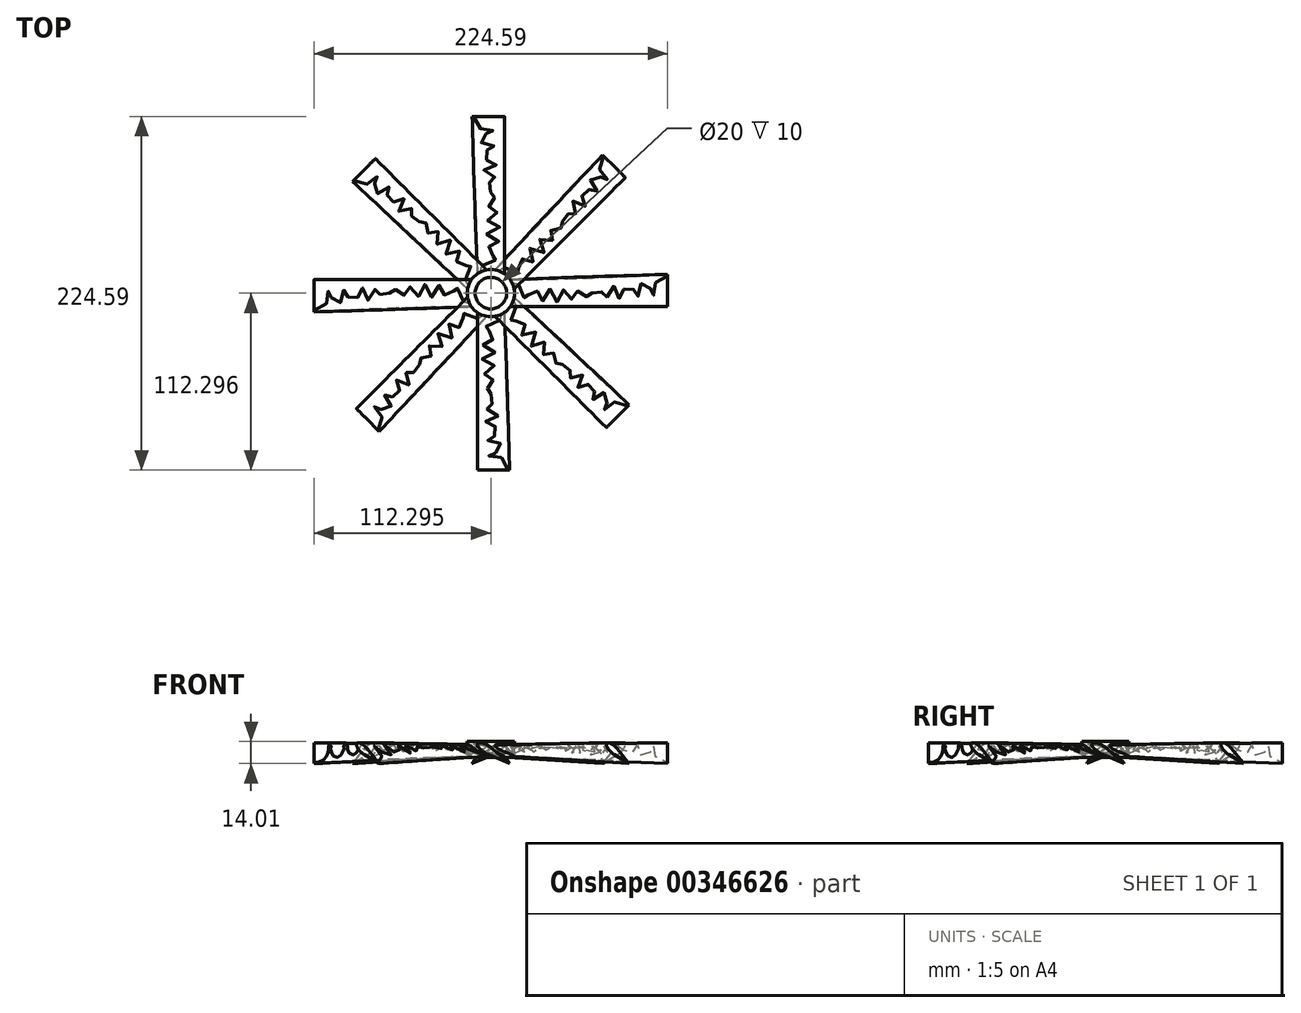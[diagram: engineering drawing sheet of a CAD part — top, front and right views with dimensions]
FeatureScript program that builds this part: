
annotation { "Feature Type Name" : "Feature", "Feature Type Description" : "" }
export const myFeature = defineFeature(function(context is Context, id is Id, definition is map)
    precondition{}
    {
        {
            var Q0;
            Q0=qCreatedBy(makeId("Right.planeOp"),FACE);
            var sketch = newSketch(context, id + "F0", { "sketchPlane" : qUnion([Q0])});
            skCircle(sketch, "E0", {"center": v(0, 0) * mm, "radius": 5 * mm});
            skPoint(sketch, "E1", {"position": v(3.38, 3.68) * mm});
            skPoint(sketch, "E2", {"position": v(-2.55, 4.3) * mm});
            skPoint(sketch, "E3", {"position": v(-4.58, 2) * mm});
            skPoint(sketch, "E4", {"position": v(-3.59, -3.48) * mm});
            skPoint(sketch, "E5", {"position": v(1.45, -4.79) * mm});
            skLineSegment(sketch, "E6", {"start": v(0, 11.08) * mm, "end": v(0, 16.41) * mm, "construction": true});
            skSolve(sketch);
        }
        {
            var Q0;
            Q0=qCreatedBy(makeId("Right.planeOp"),FACE);
            cPlane(context, id + "F1", {"entities" : qUnion([Q0]), "cplaneType" : CPlaneType.OFFSET, "offset" : 10 * mm, "width" : 150 * mm, "height" : 150 * mm});
        }
        {
            var Q0;
            Q0=qCreatedBy(id+"F1.planeOp",FACE);
            var sketch = newSketch(context, id + "F2", { "sketchPlane" : qUnion([Q0])});
            skCircle(sketch, "E7", {"center": v(0, 0) * mm, "radius": 5 * mm});
            skPoint(sketch, "E8", {"position": v(3.38, 3.68) * mm});
            skPoint(sketch, "E9", {"position": v(-2.55, 4.3) * mm});
            skPoint(sketch, "E10", {"position": v(-4.58, 2) * mm});
            skPoint(sketch, "E11", {"position": v(-3.59, -3.48) * mm});
            skPoint(sketch, "E12", {"position": v(1.45, -4.79) * mm});
            skSolve(sketch);
        }
        {
            var Q0;
            Q0=qCreatedBy(makeId("Right.planeOp"),FACE);
            cPlane(context, id + "F3", {"entities" : qUnion([Q0]), "cplaneType" : CPlaneType.OFFSET, "offset" : 20 * mm, "width" : 150 * mm, "height" : 150 * mm});
        }
        {
            var Q0;
            Q0=qCreatedBy(id+"F3.planeOp",FACE);
            var sketch = newSketch(context, id + "F4", { "sketchPlane" : qUnion([Q0])});
            skLineSegment(sketch, "E13", {"start": v(11.65, 0) * mm, "end": v(19.56, 0) * mm, "construction": true});
            skLineSegment(sketch, "E14", {"start": v(-14.42, -9) * mm, "end": v(5.84, 3.65) * mm, "construction": true});
            skPoint(sketch, "E15", {"position": v(0.08, 0.05) * mm});
            skEllipse(sketch, "E16", {"center": v(0.08, 0.05) * mm, "majorRadius": 6.78 * mm, "minorRadius": 2.5 * mm, "majorAxis": v(0.85, 0.53)});
            skLineSegment(sketch, "E17", {"start": v(0.08, 0.05) * mm, "end": v(-1.24, 2.17) * mm, "construction": true});
            skLineSegment(sketch, "E18", {"start": v(-14.42, -9) * mm, "end": v(-3.41, 0.57) * mm});
            skLineSegment(sketch, "E19", {"start": v(-14.42, -9) * mm, "end": v(-0.98, -3.32) * mm});
            skPoint(sketch, "E20", {"position": v(0, 0) * mm});
            skSolve(sketch);
        }
        {
            var Q0;
            Q0=qCreatedBy(makeId("Right.planeOp"),FACE);
            cPlane(context, id + "F5", {"entities" : qUnion([Q0]), "cplaneType" : CPlaneType.OFFSET, "offset" : 25 * mm, "width" : 150 * mm, "height" : 150 * mm});
        }
        {
            var Q0;
            Q0=qCreatedBy(id+"F5.planeOp",FACE);
            var sketch = newSketch(context, id + "F6", { "sketchPlane" : qUnion([Q0])});
            skLineSegment(sketch, "E21", {"start": v(11.65, 0) * mm, "end": v(19.56, 0) * mm, "construction": true});
            skLineSegment(sketch, "E22", {"start": v(-14.28, -8.75) * mm, "end": v(3.41, 2.09) * mm, "construction": true});
            skPoint(sketch, "E23", {"position": v(0.09, 0.05) * mm});
            skEllipse(sketch, "E24", {"center": v(0.09, 0.05) * mm, "majorRadius": 3.9 * mm, "minorRadius": 2.3 * mm, "majorAxis": v(0.85, 0.52)});
            skLineSegment(sketch, "E25", {"start": v(0.09, 0.05) * mm, "end": v(-1.12, 2.01) * mm, "construction": true});
            skLineSegment(sketch, "E26", {"start": v(-14.28, -8.75) * mm, "end": v(-1.85, 1.49) * mm});
            skLineSegment(sketch, "E27", {"start": v(-14.28, -8.75) * mm, "end": v(0.48, -2.33) * mm});
            skPoint(sketch, "E28", {"position": v(0, 0) * mm});
            skSolve(sketch);
        }
        {
            var Q0;
            Q0=qCreatedBy(makeId("Right.planeOp"),FACE);
            cPlane(context, id + "F7", {"entities" : qUnion([Q0]), "cplaneType" : CPlaneType.OFFSET, "offset" : 30 * mm, "width" : 150 * mm, "height" : 150 * mm});
        }
        {
            var Q0;
            Q0=qCreatedBy(id+"F7.planeOp",FACE);
            var sketch = newSketch(context, id + "F8", { "sketchPlane" : qUnion([Q0])});
            skLineSegment(sketch, "E29", {"start": v(11.65, 0) * mm, "end": v(19.56, 0) * mm, "construction": true});
            skLineSegment(sketch, "E30", {"start": v(-14.14, -8.5) * mm, "end": v(5.57, 3.35) * mm, "construction": true});
            skPoint(sketch, "E31", {"position": v(0.17, 0.1) * mm});
            skEllipse(sketch, "E32", {"center": v(0.17, 0.1) * mm, "majorRadius": 6.3 * mm, "minorRadius": 2.4 * mm, "majorAxis": v(0.86, 0.52)});
            skLineSegment(sketch, "E33", {"start": v(0.17, 0.1) * mm, "end": v(-1.06, 2.16) * mm, "construction": true});
            skLineSegment(sketch, "E34", {"start": v(-14.14, -8.5) * mm, "end": v(-3.01, 0.78) * mm});
            skLineSegment(sketch, "E35", {"start": v(-14.14, -8.5) * mm, "end": v(-0.72, -3.03) * mm});
            skPoint(sketch, "E36", {"position": v(0, 0) * mm});
            skSolve(sketch);
        }
        {
            var Q0;
            Q0=qCreatedBy(makeId("Right.planeOp"),FACE);
            cPlane(context, id + "F9", {"entities" : qUnion([Q0]), "cplaneType" : CPlaneType.OFFSET, "offset" : 35 * mm, "width" : 150 * mm, "height" : 150 * mm});
        }
        {
            var Q0;
            Q0=qCreatedBy(id+"F9.planeOp",FACE);
            var sketch = newSketch(context, id + "F10", { "sketchPlane" : qUnion([Q0])});
            skLineSegment(sketch, "E37", {"start": v(11.65, 0) * mm, "end": v(19.56, 0) * mm, "construction": true});
            skLineSegment(sketch, "E38", {"start": v(-14, -8.25) * mm, "end": v(3.45, 2.03) * mm, "construction": true});
            skPoint(sketch, "E39", {"position": v(0.09, 0.05) * mm});
            skEllipse(sketch, "E40", {"center": v(0.09, 0.05) * mm, "majorRadius": 3.9 * mm, "minorRadius": 2.2 * mm, "majorAxis": v(0.86, 0.5)});
            skLineSegment(sketch, "E41", {"start": v(0.09, 0.05) * mm, "end": v(-1.03, 1.95) * mm, "construction": true});
            skLineSegment(sketch, "E42", {"start": v(-14, -8.25) * mm, "end": v(-1.8, 1.42) * mm});
            skLineSegment(sketch, "E43", {"start": v(-14, -8.25) * mm, "end": v(0.37, -2.26) * mm});
            skPoint(sketch, "E44", {"position": v(0, 0) * mm});
            skSolve(sketch);
        }
        {
            var Q0;
            Q0=qCreatedBy(makeId("Right.planeOp"),FACE);
            cPlane(context, id + "F11", {"entities" : qUnion([Q0]), "cplaneType" : CPlaneType.OFFSET, "offset" : 40 * mm, "width" : 150 * mm, "height" : 150 * mm});
        }
        {
            var Q0;
            Q0=qCreatedBy(id+"F11.planeOp",FACE);
            var sketch = newSketch(context, id + "F12", { "sketchPlane" : qUnion([Q0])});
            skLineSegment(sketch, "E45", {"start": v(11.65, 0) * mm, "end": v(19.56, 0) * mm, "construction": true});
            skLineSegment(sketch, "E46", {"start": v(-13.86, -8) * mm, "end": v(5.63, 3.25) * mm, "construction": true});
            skPoint(sketch, "E47", {"position": v(0.26, 0.15) * mm});
            skEllipse(sketch, "E48", {"center": v(0.26, 0.15) * mm, "majorRadius": 6.2 * mm, "minorRadius": 2.3 * mm, "majorAxis": v(0.87, 0.5)});
            skLineSegment(sketch, "E49", {"start": v(0.26, 0.15) * mm, "end": v(-0.9, 2.14) * mm, "construction": true});
            skLineSegment(sketch, "E50", {"start": v(-13.86, -8) * mm, "end": v(-2.85, 0.81) * mm});
            skLineSegment(sketch, "E51", {"start": v(-13.86, -8) * mm, "end": v(-0.72, -2.87) * mm});
            skPoint(sketch, "E52", {"position": v(0, 0) * mm});
            skSolve(sketch);
        }
        {
            var Q0;
            Q0=qCreatedBy(makeId("Right.planeOp"),FACE);
            cPlane(context, id + "F13", {"entities" : qUnion([Q0]), "cplaneType" : CPlaneType.OFFSET, "offset" : 45 * mm, "width" : 150 * mm, "height" : 150 * mm});
        }
        {
            var Q0;
            Q0=qCreatedBy(id+"F13.planeOp",FACE);
            var sketch = newSketch(context, id + "F14", { "sketchPlane" : qUnion([Q0])});
            skLineSegment(sketch, "E53", {"start": v(11.65, 0) * mm, "end": v(19.56, 0) * mm, "construction": true});
            skLineSegment(sketch, "E54", {"start": v(-13.7, -7.76) * mm, "end": v(3.48, 1.97) * mm, "construction": true});
            skPoint(sketch, "E55", {"position": v(0.09, 0.05) * mm});
            skEllipse(sketch, "E56", {"center": v(0.09, 0.05) * mm, "majorRadius": 3.9 * mm, "minorRadius": 2.1 * mm, "majorAxis": v(0.87, 0.5)});
            skLineSegment(sketch, "E57", {"start": v(0.09, 0.05) * mm, "end": v(-0.95, 1.88) * mm, "construction": true});
            skLineSegment(sketch, "E58", {"start": v(-13.7, -7.76) * mm, "end": v(-1.75, 1.35) * mm});
            skLineSegment(sketch, "E59", {"start": v(-13.7, -7.76) * mm, "end": v(0.25, -2.2) * mm});
            skPoint(sketch, "E60", {"position": v(0, 0) * mm});
            skSolve(sketch);
        }
        {
            var Q0;
            Q0=qCreatedBy(makeId("Right.planeOp"),FACE);
            cPlane(context, id + "F15", {"entities" : qUnion([Q0]), "cplaneType" : CPlaneType.OFFSET, "offset" : 50 * mm, "width" : 150 * mm, "height" : 150 * mm});
        }
        {
            var Q0;
            Q0=qCreatedBy(id+"F15.planeOp",FACE);
            var sketch = newSketch(context, id + "F16", { "sketchPlane" : qUnion([Q0])});
            skLineSegment(sketch, "E61", {"start": v(11.65, 0) * mm, "end": v(19.56, 0) * mm, "construction": true});
            skLineSegment(sketch, "E62", {"start": v(-13.56, -7.51) * mm, "end": v(5.69, 3.15) * mm, "construction": true});
            skPoint(sketch, "E63", {"position": v(0.35, 0.2) * mm});
            skEllipse(sketch, "E64", {"center": v(0.35, 0.2) * mm, "majorRadius": 6.1 * mm, "minorRadius": 2.2 * mm, "majorAxis": v(0.87, 0.48)});
            skLineSegment(sketch, "E65", {"start": v(0.35, 0.2) * mm, "end": v(-0.72, 2.12) * mm, "construction": true});
            skLineSegment(sketch, "E66", {"start": v(-13.56, -7.51) * mm, "end": v(-2.68, 0.84) * mm});
            skLineSegment(sketch, "E67", {"start": v(-13.56, -7.51) * mm, "end": v(-0.71, -2.72) * mm});
            skPoint(sketch, "E68", {"position": v(0, 0) * mm});
            skSolve(sketch);
        }
        {
            var Q0;
            Q0=qCreatedBy(makeId("Right.planeOp"),FACE);
            cPlane(context, id + "F17", {"entities" : qUnion([Q0]), "cplaneType" : CPlaneType.OFFSET, "offset" : 55 * mm, "width" : 150 * mm, "height" : 150 * mm});
        }
        {
            var Q0;
            Q0=qCreatedBy(id+"F17.planeOp",FACE);
            var sketch = newSketch(context, id + "F18", { "sketchPlane" : qUnion([Q0])});
            skLineSegment(sketch, "E69", {"start": v(11.65, 0) * mm, "end": v(19.56, 0) * mm, "construction": true});
            skLineSegment(sketch, "E70", {"start": v(-13.4, -7.28) * mm, "end": v(3.52, 1.9) * mm, "construction": true});
            skPoint(sketch, "E71", {"position": v(0.09, 0.05) * mm});
            skEllipse(sketch, "E72", {"center": v(0.09, 0.05) * mm, "majorRadius": 3.9 * mm, "minorRadius": 2 * mm, "majorAxis": v(0.88, 0.48)});
            skLineSegment(sketch, "E73", {"start": v(0.09, 0.05) * mm, "end": v(-0.87, 1.8) * mm, "construction": true});
            skLineSegment(sketch, "E74", {"start": v(-13.4, -7.28) * mm, "end": v(-1.7, 1.27) * mm});
            skLineSegment(sketch, "E75", {"start": v(-13.4, -7.28) * mm, "end": v(0.14, -2.13) * mm});
            skPoint(sketch, "E76", {"position": v(0, 0) * mm});
            skSolve(sketch);
        }
        {
            var Q0;
            Q0=qCreatedBy(makeId("Right.planeOp"),FACE);
            cPlane(context, id + "F19", {"entities" : qUnion([Q0]), "cplaneType" : CPlaneType.OFFSET, "offset" : 60 * mm, "width" : 150 * mm, "height" : 150 * mm});
        }
        {
            var Q0;
            Q0=qCreatedBy(id+"F19.planeOp",FACE);
            var sketch = newSketch(context, id + "F20", { "sketchPlane" : qUnion([Q0])});
            skLineSegment(sketch, "E77", {"start": v(11.65, 0) * mm, "end": v(19.56, 0) * mm, "construction": true});
            skLineSegment(sketch, "E78", {"start": v(-13.24, -7.04) * mm, "end": v(5.74, 3.05) * mm, "construction": true});
            skPoint(sketch, "E79", {"position": v(0.44, 0.23) * mm});
            skEllipse(sketch, "E80", {"center": v(0.44, 0.23) * mm, "majorRadius": 6 * mm, "minorRadius": 2.1 * mm, "majorAxis": v(0.88, 0.47)});
            skLineSegment(sketch, "E81", {"start": v(0.44, 0.23) * mm, "end": v(-0.54, 2.09) * mm, "construction": true});
            skLineSegment(sketch, "E82", {"start": v(-13.24, -7.04) * mm, "end": v(-2.52, 0.85) * mm});
            skLineSegment(sketch, "E83", {"start": v(-13.24, -7.04) * mm, "end": v(-0.7, -2.57) * mm});
            skPoint(sketch, "E84", {"position": v(0, 0) * mm});
            skSolve(sketch);
        }
        {
            var Q0;
            Q0=qCreatedBy(makeId("Right.planeOp"),FACE);
            cPlane(context, id + "F21", {"entities" : qUnion([Q0]), "cplaneType" : CPlaneType.OFFSET, "offset" : 65 * mm, "width" : 150 * mm, "height" : 150 * mm});
        }
        {
            var Q0;
            Q0=qCreatedBy(id+"F21.planeOp",FACE);
            var sketch = newSketch(context, id + "F22", { "sketchPlane" : qUnion([Q0])});
            skLineSegment(sketch, "E85", {"start": v(11.65, 0) * mm, "end": v(19.56, 0) * mm, "construction": true});
            skLineSegment(sketch, "E86", {"start": v(-13.08, -6.81) * mm, "end": v(3.55, 1.85) * mm, "construction": true});
            skPoint(sketch, "E87", {"position": v(0.09, 0.05) * mm});
            skEllipse(sketch, "E88", {"center": v(0.09, 0.05) * mm, "majorRadius": 3.9 * mm, "minorRadius": 1.9 * mm, "majorAxis": v(0.89, 0.46)});
            skLineSegment(sketch, "E89", {"start": v(0.09, 0.05) * mm, "end": v(-0.79, 1.73) * mm, "construction": true});
            skLineSegment(sketch, "E90", {"start": v(-13.08, -6.81) * mm, "end": v(-1.67, 1.2) * mm});
            skLineSegment(sketch, "E91", {"start": v(-13.08, -6.81) * mm, "end": v(0.03, -2.05) * mm});
            skPoint(sketch, "E92", {"position": v(0, 0) * mm});
            skSolve(sketch);
        }
        {
            var Q0;
            Q0=qCreatedBy(makeId("Right.planeOp"),FACE);
            cPlane(context, id + "F23", {"entities" : qUnion([Q0]), "cplaneType" : CPlaneType.OFFSET, "offset" : 70 * mm, "width" : 150 * mm, "height" : 150 * mm});
        }
        {
            var Q0;
            Q0=qCreatedBy(id+"F23.planeOp",FACE);
            var sketch = newSketch(context, id + "F24", { "sketchPlane" : qUnion([Q0])});
            skLineSegment(sketch, "E93", {"start": v(11.65, 0) * mm, "end": v(19.56, 0) * mm, "construction": true});
            skLineSegment(sketch, "E94", {"start": v(-12.92, -6.58) * mm, "end": v(5.8, 2.95) * mm, "construction": true});
            skPoint(sketch, "E95", {"position": v(0.53, 0.27) * mm});
            skEllipse(sketch, "E96", {"center": v(0.53, 0.27) * mm, "majorRadius": 5.9 * mm, "minorRadius": 2 * mm, "majorAxis": v(0.9, 0.45)});
            skLineSegment(sketch, "E97", {"start": v(0.53, 0.27) * mm, "end": v(-0.37, 2.05) * mm, "construction": true});
            skLineSegment(sketch, "E98", {"start": v(-12.92, -6.58) * mm, "end": v(-2.36, 0.87) * mm});
            skLineSegment(sketch, "E99", {"start": v(-12.92, -6.58) * mm, "end": v(-0.68, -2.41) * mm});
            skPoint(sketch, "E100", {"position": v(0, 0) * mm});
            skSolve(sketch);
        }
        {
            var Q0;
            Q0=qCreatedBy(makeId("Right.planeOp"),FACE);
            cPlane(context, id + "F25", {"entities" : qUnion([Q0]), "cplaneType" : CPlaneType.OFFSET, "offset" : 75 * mm, "width" : 150 * mm, "height" : 150 * mm});
        }
        {
            var Q0;
            Q0=qCreatedBy(id+"F25.planeOp",FACE);
            var sketch = newSketch(context, id + "F26", { "sketchPlane" : qUnion([Q0])});
            skLineSegment(sketch, "E101", {"start": v(11.65, 0) * mm, "end": v(19.56, 0) * mm, "construction": true});
            skLineSegment(sketch, "E102", {"start": v(-12.75, -6.36) * mm, "end": v(3.58, 1.78) * mm, "construction": true});
            skPoint(sketch, "E103", {"position": v(0.09, 0.04) * mm});
            skEllipse(sketch, "E104", {"center": v(0.09, 0.04) * mm, "majorRadius": 3.9 * mm, "minorRadius": 1.8 * mm, "majorAxis": v(0.9, 0.45)});
            skLineSegment(sketch, "E105", {"start": v(0.09, 0.04) * mm, "end": v(-0.71, 1.66) * mm, "construction": true});
            skLineSegment(sketch, "E106", {"start": v(-12.75, -6.36) * mm, "end": v(-1.63, 1.12) * mm});
            skLineSegment(sketch, "E107", {"start": v(-12.75, -6.36) * mm, "end": v(-0.09, -1.98) * mm});
            skPoint(sketch, "E108", {"position": v(0, 0) * mm});
            skSolve(sketch);
        }
        {
            var Q0;
            Q0=qCreatedBy(makeId("Right.planeOp"),FACE);
            cPlane(context, id + "F27", {"entities" : qUnion([Q0]), "cplaneType" : CPlaneType.OFFSET, "offset" : 80 * mm, "width" : 150 * mm, "height" : 150 * mm});
        }
        {
            var Q0;
            Q0=qCreatedBy(id+"F27.planeOp",FACE);
            var sketch = newSketch(context, id + "F28", { "sketchPlane" : qUnion([Q0])});
            skLineSegment(sketch, "E109", {"start": v(11.65, 0) * mm, "end": v(19.56, 0) * mm, "construction": true});
            skLineSegment(sketch, "E110", {"start": v(-12.58, -6.14) * mm, "end": v(5.84, 2.85) * mm, "construction": true});
            skPoint(sketch, "E111", {"position": v(0.63, 0.3) * mm});
            skEllipse(sketch, "E112", {"center": v(0.63, 0.3) * mm, "majorRadius": 5.8 * mm, "minorRadius": 1.9 * mm, "majorAxis": v(0.9, 0.44)});
            skLineSegment(sketch, "E113", {"start": v(0.63, 0.3) * mm, "end": v(-0.2, 2.01) * mm, "construction": true});
            skLineSegment(sketch, "E114", {"start": v(-12.58, -6.14) * mm, "end": v(-2.2, 0.87) * mm});
            skLineSegment(sketch, "E115", {"start": v(-12.58, -6.14) * mm, "end": v(-0.66, -2.27) * mm});
            skPoint(sketch, "E116", {"position": v(0, 0) * mm});
            skSolve(sketch);
        }
        {
            var Q0;
            Q0=qCreatedBy(makeId("Right.planeOp"),FACE);
            cPlane(context, id + "F29", {"entities" : qUnion([Q0]), "cplaneType" : CPlaneType.OFFSET, "offset" : 85 * mm, "width" : 150 * mm, "height" : 150 * mm});
        }
        {
            var Q0;
            Q0=qCreatedBy(id+"F29.planeOp",FACE);
            var sketch = newSketch(context, id + "F30", { "sketchPlane" : qUnion([Q0])});
            skLineSegment(sketch, "E117", {"start": v(11.65, 0) * mm, "end": v(19.56, 0) * mm, "construction": true});
            skLineSegment(sketch, "E118", {"start": v(-12.41, -5.92) * mm, "end": v(3.61, 1.72) * mm, "construction": true});
            skPoint(sketch, "E119", {"position": v(0.1, 0.04) * mm});
            skEllipse(sketch, "E120", {"center": v(0.1, 0.04) * mm, "majorRadius": 3.9 * mm, "minorRadius": 1.7 * mm, "majorAxis": v(0.9, 0.43)});
            skLineSegment(sketch, "E121", {"start": v(0.1, 0.04) * mm, "end": v(-0.64, 1.58) * mm, "construction": true});
            skLineSegment(sketch, "E122", {"start": v(-12.41, -5.92) * mm, "end": v(-1.6, 1.04) * mm});
            skLineSegment(sketch, "E123", {"start": v(-12.41, -5.92) * mm, "end": v(-0.2, -1.9) * mm});
            skPoint(sketch, "E124", {"position": v(0, 0) * mm});
            skSolve(sketch);
        }
        {
            var Q0;
            Q0=qCreatedBy(makeId("Right.planeOp"),FACE);
            cPlane(context, id + "F31", {"entities" : qUnion([Q0]), "cplaneType" : CPlaneType.OFFSET, "offset" : 90 * mm, "width" : 150 * mm, "height" : 150 * mm});
        }
        {
            var Q0;
            Q0=qCreatedBy(id+"F31.planeOp",FACE);
            var sketch = newSketch(context, id + "F32", { "sketchPlane" : qUnion([Q0])});
            skLineSegment(sketch, "E125", {"start": v(11.65, 0) * mm, "end": v(19.56, 0) * mm, "construction": true});
            skLineSegment(sketch, "E126", {"start": v(-12.24, -5.7) * mm, "end": v(5.9, 2.75) * mm, "construction": true});
            skPoint(sketch, "E127", {"position": v(0.73, 0.34) * mm});
            skEllipse(sketch, "E128", {"center": v(0.73, 0.34) * mm, "majorRadius": 5.7 * mm, "minorRadius": 1.8 * mm, "majorAxis": v(0.9, 0.42)});
            skLineSegment(sketch, "E129", {"start": v(0.73, 0.34) * mm, "end": v(-0.04, 1.97) * mm, "construction": true});
            skLineSegment(sketch, "E130", {"start": v(-12.24, -5.7) * mm, "end": v(-2.03, 0.87) * mm});
            skLineSegment(sketch, "E131", {"start": v(-12.24, -5.7) * mm, "end": v(-0.64, -2.12) * mm});
            skPoint(sketch, "E132", {"position": v(0, 0) * mm});
            skSolve(sketch);
        }
        {
            var Q0;
            Q0=qCreatedBy(makeId("Right.planeOp"),FACE);
            cPlane(context, id + "F33", {"entities" : qUnion([Q0]), "cplaneType" : CPlaneType.OFFSET, "offset" : 95 * mm, "width" : 150 * mm, "height" : 150 * mm});
        }
        {
            var Q0;
            Q0=qCreatedBy(id+"F33.planeOp",FACE);
            var sketch = newSketch(context, id + "F34", { "sketchPlane" : qUnion([Q0])});
            skLineSegment(sketch, "E133", {"start": v(11.65, 0) * mm, "end": v(19.56, 0) * mm, "construction": true});
            skLineSegment(sketch, "E134", {"start": v(-12.06, -5.5) * mm, "end": v(3.64, 1.66) * mm, "construction": true});
            skPoint(sketch, "E135", {"position": v(0.1, 0.04) * mm});
            skEllipse(sketch, "E136", {"center": v(0.1, 0.04) * mm, "majorRadius": 3.9 * mm, "minorRadius": 1.6 * mm, "majorAxis": v(0.9, 0.41)});
            skLineSegment(sketch, "E137", {"start": v(0.1, 0.04) * mm, "end": v(-0.57, 1.5) * mm, "construction": true});
            skLineSegment(sketch, "E138", {"start": v(-12.06, -5.5) * mm, "end": v(-1.58, 0.96) * mm});
            skLineSegment(sketch, "E139", {"start": v(-12.06, -5.5) * mm, "end": v(-0.31, -1.82) * mm});
            skPoint(sketch, "E140", {"position": v(0, 0) * mm});
            skSolve(sketch);
        }
        {
            var Q0;
            Q0=qCreatedBy(makeId("Right.planeOp"),FACE);
            cPlane(context, id + "F35", {"entities" : qUnion([Q0]), "cplaneType" : CPlaneType.OFFSET, "offset" : 100 * mm, "width" : 150 * mm, "height" : 150 * mm});
        }
        {
            var Q0;
            Q0=qCreatedBy(id+"F35.planeOp",FACE);
            var sketch = newSketch(context, id + "F36", { "sketchPlane" : qUnion([Q0])});
            skLineSegment(sketch, "E141", {"start": v(11.65, 0) * mm, "end": v(19.56, 0) * mm, "construction": true});
            skLineSegment(sketch, "E142", {"start": v(-11.88, -5.29) * mm, "end": v(5.94, 2.64) * mm, "construction": true});
            skPoint(sketch, "E143", {"position": v(0.82, 0.37) * mm});
            skEllipse(sketch, "E144", {"center": v(0.82, 0.37) * mm, "majorRadius": 5.6 * mm, "minorRadius": 1.7 * mm, "majorAxis": v(0.91, 0.4)});
            skLineSegment(sketch, "E145", {"start": v(0.82, 0.37) * mm, "end": v(0.13, 1.92) * mm, "construction": true});
            skLineSegment(sketch, "E146", {"start": v(-11.88, -5.29) * mm, "end": v(-1.87, 0.87) * mm});
            skLineSegment(sketch, "E147", {"start": v(-11.88, -5.29) * mm, "end": v(-0.6, -1.97) * mm});
            skPoint(sketch, "E148", {"position": v(0, 0) * mm});
            skSolve(sketch);
        }
        {
            var Q0;
            Q0=qCreatedBy(makeId("Right.planeOp"),FACE);
            cPlane(context, id + "F37", {"entities" : qUnion([Q0]), "cplaneType" : CPlaneType.OFFSET, "offset" : 105 * mm, "width" : 150 * mm, "height" : 150 * mm});
        }
        {
            var Q0;
            Q0=qCreatedBy(id+"F37.planeOp",FACE);
            var sketch = newSketch(context, id + "F38", { "sketchPlane" : qUnion([Q0])});
            skLineSegment(sketch, "E149", {"start": v(11.65, 0) * mm, "end": v(19.56, 0) * mm, "construction": true});
            skLineSegment(sketch, "E150", {"start": v(-11.7, -5.08) * mm, "end": v(3.67, 1.6) * mm, "construction": true});
            skPoint(sketch, "E151", {"position": v(0.1, 0.04) * mm});
            skEllipse(sketch, "E152", {"center": v(0.1, 0.04) * mm, "majorRadius": 3.9 * mm, "minorRadius": 1.5 * mm, "majorAxis": v(0.92, 0.4)});
            skLineSegment(sketch, "E153", {"start": v(0.1, 0.04) * mm, "end": v(-0.5, 1.42) * mm, "construction": true});
            skLineSegment(sketch, "E154", {"start": v(-11.7, -5.08) * mm, "end": v(-1.56, 0.88) * mm});
            skLineSegment(sketch, "E155", {"start": v(-11.7, -5.08) * mm, "end": v(-0.42, -1.74) * mm});
            skPoint(sketch, "E156", {"position": v(0, 0) * mm});
            skSolve(sketch);
        }
        {
            var Q0;
            Q0=qCreatedBy(makeId("Right.planeOp"),FACE);
            cPlane(context, id + "F39", {"entities" : qUnion([Q0]), "cplaneType" : CPlaneType.OFFSET, "offset" : 110 * mm, "width" : 150 * mm, "height" : 150 * mm});
        }
        {
            var Q0;
            Q0=qCreatedBy(id+"F39.planeOp",FACE);
            var sketch = newSketch(context, id + "F40", { "sketchPlane" : qUnion([Q0])});
            skLineSegment(sketch, "E157", {"start": v(11.65, 0) * mm, "end": v(19.56, 0) * mm, "construction": true});
            skLineSegment(sketch, "E158", {"start": v(-11.5, -4.88) * mm, "end": v(5.98, 2.54) * mm, "construction": true});
            skPoint(sketch, "E159", {"position": v(0.92, 0.4) * mm});
            skEllipse(sketch, "E160", {"center": v(0.92, 0.4) * mm, "majorRadius": 5.5 * mm, "minorRadius": 1.6 * mm, "majorAxis": v(0.92, 0.4)});
            skLineSegment(sketch, "E161", {"start": v(0.92, 0.4) * mm, "end": v(0.3, 1.86) * mm, "construction": true});
            skLineSegment(sketch, "E162", {"start": v(-11.5, -4.88) * mm, "end": v(-1.71, 0.86) * mm});
            skLineSegment(sketch, "E163", {"start": v(-11.5, -4.88) * mm, "end": v(-0.57, -1.83) * mm});
            skPoint(sketch, "E164", {"position": v(0, 0) * mm});
            skSolve(sketch);
        }
        {
            var Q0;
            Q0=qCreatedBy(makeId("Right.planeOp"),FACE);
            cPlane(context, id + "F41", {"entities" : qUnion([Q0]), "cplaneType" : CPlaneType.OFFSET, "offset" : 115 * mm, "width" : 150 * mm, "height" : 150 * mm});
        }
        {
            var Q0;
            Q0=qCreatedBy(id+"F41.planeOp",FACE);
            var sketch = newSketch(context, id + "F42", { "sketchPlane" : qUnion([Q0])});
            skLineSegment(sketch, "E165", {"start": v(11.65, 0) * mm, "end": v(19.56, 0) * mm, "construction": true});
            skLineSegment(sketch, "E166", {"start": v(-11.32, -4.69) * mm, "end": v(3.7, 1.53) * mm, "construction": true});
            skPoint(sketch, "E167", {"position": v(0.1, 0.04) * mm});
            skEllipse(sketch, "E168", {"center": v(0.1, 0.04) * mm, "majorRadius": 3.9 * mm, "minorRadius": 1.4 * mm, "majorAxis": v(0.92, 0.38)});
            skLineSegment(sketch, "E169", {"start": v(0.1, 0.04) * mm, "end": v(-0.44, 1.33) * mm, "construction": true});
            skLineSegment(sketch, "E170", {"start": v(-11.32, -4.69) * mm, "end": v(-1.55, 0.8) * mm});
            skLineSegment(sketch, "E171", {"start": v(-11.32, -4.69) * mm, "end": v(-0.54, -1.66) * mm});
            skPoint(sketch, "E172", {"position": v(0, 0) * mm});
            skSolve(sketch);
        }
        {
            var Q0;
            Q0=qCreatedBy(makeId("Right.planeOp"),FACE);
            cPlane(context, id + "F43", {"entities" : qUnion([Q0]), "cplaneType" : CPlaneType.OFFSET, "offset" : 120 * mm, "width" : 150 * mm, "height" : 150 * mm});
        }
        {
            var Q0;
            Q0=qCreatedBy(id+"F43.planeOp",FACE);
            var sketch = newSketch(context, id + "F44", { "sketchPlane" : qUnion([Q0])});
            skLineSegment(sketch, "E173", {"start": v(11.65, 0) * mm, "end": v(19.56, 0) * mm, "construction": true});
            skLineSegment(sketch, "E174", {"start": v(-11.13, -4.5) * mm, "end": v(6.03, 2.43) * mm, "construction": true});
            skPoint(sketch, "E175", {"position": v(1.02, 0.41) * mm});
            skEllipse(sketch, "E176", {"center": v(1.02, 0.41) * mm, "majorRadius": 5.4 * mm, "minorRadius": 1.5 * mm, "majorAxis": v(0.93, 0.37)});
            skLineSegment(sketch, "E177", {"start": v(1.02, 0.41) * mm, "end": v(0.46, 1.8) * mm, "construction": true});
            skLineSegment(sketch, "E178", {"start": v(-11.13, -4.5) * mm, "end": v(-1.56, 0.85) * mm});
            skLineSegment(sketch, "E179", {"start": v(-11.13, -4.5) * mm, "end": v(-0.53, -1.69) * mm});
            skPoint(sketch, "E180", {"position": v(0, 0) * mm});
            skLineSegment(sketch, "E181", {"start": v(0, 10.3) * mm, "end": v(0, 18.2) * mm, "construction": true});
            skSolve(sketch);
        }
        {
            var Q0;
            Q0 = qSketchRegion(id + "F4", true);
            var Q1;
            Q1 = qSketchRegion(id + "F6", true);
            var Q2;
            Q2 = qSketchRegion(id + "F8", true);
            var Q3;
            Q3 = qSketchRegion(id + "F10", true);
            var Q4;
            Q4 = qSketchRegion(id + "F12", true);
            var Q5;
            Q5 = qSketchRegion(id + "F14", true);
            var Q6;
            Q6 = qSketchRegion(id + "F16", true);
            var Q7;
            Q7 = qSketchRegion(id + "F18", true);
            var Q8;
            Q8 = qSketchRegion(id + "F20", true);
            var Q9;
            Q9 = qSketchRegion(id + "F22", true);
            var Q10;
            Q10 = qSketchRegion(id + "F24", true);
            var Q11;
            Q11 = qSketchRegion(id + "F26", true);
            var Q12;
            Q12 = qSketchRegion(id + "F28", true);
            var Q13;
            Q13 = qSketchRegion(id + "F30", true);
            var Q14;
            Q14 = qSketchRegion(id + "F32", true);
            var Q15;
            Q15 = qSketchRegion(id + "F34", true);
            var Q16;
            Q16 = qSketchRegion(id + "F36", true);
            var Q17;
            Q17 = qSketchRegion(id + "F38", true);
            var Q18;
            Q18 = qSketchRegion(id + "F40", true);
            var Q19;
            Q19 = qSketchRegion(id + "F42", true);
            var Q20;
            Q20 = qSketchRegion(id + "F44", true);
            var Q21;
            Q21=sQuery(id+"F4.wireOp",VERTEX,"E14.end");
            var Q22;
            Q22=sQuery(id+"F6.wireOp",VERTEX,"E22.end");
            var Q23;
            Q23=sQuery(id+"F8.wireOp",VERTEX,"E30.end");
            var Q24;
            Q24=sQuery(id+"F10.wireOp",VERTEX,"E38.end");
            var Q25;
            Q25=sQuery(id+"F12.wireOp",VERTEX,"E46.end");
            var Q26;
            Q26=sQuery(id+"F14.wireOp",VERTEX,"E54.end");
            var Q27;
            Q27=sQuery(id+"F16.wireOp",VERTEX,"E62.end");
            var Q28;
            Q28=sQuery(id+"F18.wireOp",VERTEX,"E70.end");
            var Q29;
            Q29=sQuery(id+"F20.wireOp",VERTEX,"E78.end");
            var Q30;
            Q30=sQuery(id+"F22.wireOp",VERTEX,"E86.end");
            var Q31;
            Q31=sQuery(id+"F24.wireOp",VERTEX,"E94.end");
            var Q32;
            Q32=sQuery(id+"F26.wireOp",VERTEX,"E102.end");
            var Q33;
            Q33=sQuery(id+"F28.wireOp",VERTEX,"E110.end");
            var Q34;
            Q34=sQuery(id+"F30.wireOp",VERTEX,"E118.end");
            var Q35;
            Q35=sQuery(id+"F32.wireOp",VERTEX,"E126.end");
            var Q36;
            Q36=sQuery(id+"F34.wireOp",VERTEX,"E134.end");
            var Q37;
            Q37=sQuery(id+"F36.wireOp",VERTEX,"E142.end");
            var Q38;
            Q38=sQuery(id+"F38.wireOp",VERTEX,"E150.end");
            var Q39;
            Q39=sQuery(id+"F40.wireOp",VERTEX,"E158.end");
            var Q40;
            Q40=sQuery(id+"F42.wireOp",VERTEX,"E166.end");
            var Q41;
            Q41=sQuery(id+"F44.wireOp",VERTEX,"E174.end");
            loft(context, id + "F45", {"sheetProfilesArray" : [{ "sheetProfileEntities" : qUnion([Q0]) }, { "sheetProfileEntities" : qUnion([Q1]) }, { "sheetProfileEntities" : qUnion([Q2]) }, { "sheetProfileEntities" : qUnion([Q3]) }, { "sheetProfileEntities" : qUnion([Q4]) }, { "sheetProfileEntities" : qUnion([Q5]) }, { "sheetProfileEntities" : qUnion([Q6]) }, { "sheetProfileEntities" : qUnion([Q7]) }, { "sheetProfileEntities" : qUnion([Q8]) }, { "sheetProfileEntities" : qUnion([Q9]) }, { "sheetProfileEntities" : qUnion([Q10]) }, { "sheetProfileEntities" : qUnion([Q11]) }, { "sheetProfileEntities" : qUnion([Q12]) }, { "sheetProfileEntities" : qUnion([Q13]) }, { "sheetProfileEntities" : qUnion([Q14]) }, { "sheetProfileEntities" : qUnion([Q15]) }, { "sheetProfileEntities" : qUnion([Q16]) }, { "sheetProfileEntities" : qUnion([Q17]) }, { "sheetProfileEntities" : qUnion([Q18]) }, { "sheetProfileEntities" : qUnion([Q19]) }, { "sheetProfileEntities" : qUnion([Q20]) }], "matchConnections" : true, "connections" : [{ "connectionEntities" : qUnion([Q21, Q22, Q23, Q24, Q25, Q26, Q27, Q28, Q29, Q30, Q31, Q32, Q33, Q34, Q35, Q36, Q37, Q38, Q39, Q40, Q41]), "connectionEdgeQueries" : qUnion([]), "connectionEdgeParameters" : [] }]});
        }
        {
            var Q0;
            Q0 = qSketchRegion(id + "F4", true);
            var Q1;
            Q1 = qSketchRegion(id + "F44", true);
            loft(context, id + "F46", {"sheetProfilesArray" : [{ "sheetProfileEntities" : qUnion([Q0]) }, { "sheetProfileEntities" : qUnion([Q1]) }]});
        }
        {
            var Q0;
            Q0=qCreatedBy(makeId("Top.planeOp"),FACE);
            var sketch = newSketch(context, id + "F47", { "sketchPlane" : qUnion([Q0])});
            skCircle(sketch, "E182", {"center": v(0, 0) * mm, "radius": 7.5 * mm});
            skCircle(sketch, "E183", {"center": v(0, 0) * mm, "radius": 15 * mm});
            skPoint(sketch, "E184", {"position": v(120, 6.06) * mm});
            skPoint(sketch, "E185", {"position": v(120, -11.13) * mm});
            skLineSegment(sketch, "E186", {"start": v(120, 6.06) * mm, "end": v(120, -11.13) * mm, "construction": true});
            skPoint(sketch, "E187", {"position": v(120, -2.53) * mm});
            skCircle(sketch, "E188", {"center": v(132.3, -2.53) * mm, "radius": 15 * mm});
            skCircle(sketch, "E189", {"center": v(132.3, -2.53) * mm, "radius": 10 * mm});
            skSolve(sketch);
        }
        {
            var Q0;
            Q0=makeQuery(id+"F47.imprint","IMPRINT",FACE,{"disambiguationData":[TD([[makeQuery(id+"F47.imprint","IMPRINT",EDGE,{"derivedFrom":sQuery(id+"F47.wireOp",EDGE,"E188")}),1.0]])]});
            extrude(context, id + "F48", {"entities" : qUnion([Q0]), "operationType" : NewBodyOperationType.ADD, "depth" : 5 * mm, "offsetDistance" : 25 * mm, "hasSecondDirection" : true, "secondDirectionOppositeDirection" : true, "secondDirectionDepth" : 5 * mm});
        }
        {
            var Q0;
            {var subQ0=sQuery(id+"F44.wireOp",EDGE,"E176");var subQ1=makeQuery(id+"F44.imprint","INTERSECT",VERTEX,{"derivedFrom":[subQ0,sQuery(id+"F44.wireOp",EDGE,"E178")]});var subQ3=sQuery(id+"F4.wireOp",EDGE,"E16");var subQ4=makeQuery(id+"F4.imprint","INTERSECT",VERTEX,{"derivedFrom":[subQ3,sQuery(id+"F4.wireOp",EDGE,"E18")]});Q0=makeQuery(id+"F45.opLoft","SWEPT_BODY",BODY,{"disambiguationData":[OSD([makeQuery(id+"F4.imprint","IMPRINT",FACE,{"disambiguationData":[TD([[makeQuery(id+"F4.imprint","IMPRINT",EDGE,{"disambiguationData":[TD([[subQ4,-1.0]])],"derivedFrom":subQ3}),1.0]])]}),sQuery(id+"F6.wireOp",EDGE,"E26"),sQuery(id+"F8.wireOp",EDGE,"E34"),sQuery(id+"F10.wireOp",EDGE,"E42"),sQuery(id+"F12.wireOp",EDGE,"E50"),sQuery(id+"F14.wireOp",EDGE,"E58"),sQuery(id+"F16.wireOp",EDGE,"E66"),sQuery(id+"F18.wireOp",EDGE,"E74"),sQuery(id+"F20.wireOp",EDGE,"E82"),sQuery(id+"F22.wireOp",EDGE,"E90"),sQuery(id+"F24.wireOp",EDGE,"E98"),sQuery(id+"F26.wireOp",EDGE,"E106"),sQuery(id+"F28.wireOp",EDGE,"E114"),sQuery(id+"F30.wireOp",EDGE,"E122"),sQuery(id+"F32.wireOp",EDGE,"E130"),sQuery(id+"F34.wireOp",EDGE,"E138"),sQuery(id+"F36.wireOp",EDGE,"E146"),sQuery(id+"F38.wireOp",EDGE,"E154"),sQuery(id+"F40.wireOp",EDGE,"E162"),sQuery(id+"F42.wireOp",EDGE,"E170"),makeQuery(id+"F44.imprint","IMPRINT",FACE,{"disambiguationData":[TD([[makeQuery(id+"F44.imprint","IMPRINT",EDGE,{"disambiguationData":[TD([[subQ1,-1.0]])],"derivedFrom":subQ0}),1.0]])]})])]});}
            var Q1;
            Q1=sQuery(id+"F47.wireOp",EDGE,"E189");
            circularPattern(context, id + "F49", {"operationType" : NewBodyOperationType.ADD, "entities" : qUnion([Q0]), "axis" : qUnion([Q1]), "angle" : 360 * degree, "instanceCount" : 8, "equalSpace" : true});
        }
    });
